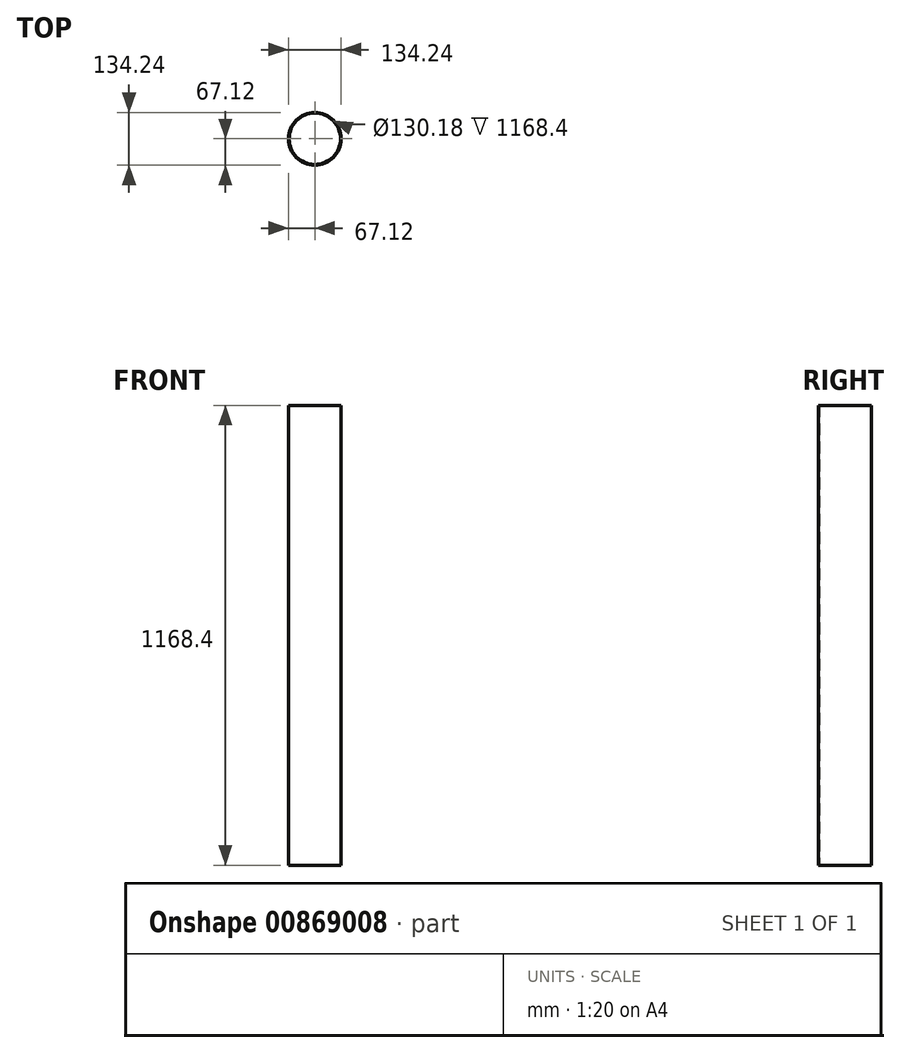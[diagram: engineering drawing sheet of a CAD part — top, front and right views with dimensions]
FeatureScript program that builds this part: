
annotation { "Feature Type Name" : "Feature", "Feature Type Description" : "" }
export const myFeature = defineFeature(function(context is Context, id is Id, definition is map)
    precondition{}
    {
        {
            var Q0;
            Q0=qCreatedBy(makeId("Top.planeOp"),FACE);
            var sketch = newSketch(context, id + "F0", { "sketchPlane" : qUnion([Q0]), "disableImprinting" : false});
            skCircle(sketch, "E0", {"center": v(0, 0) * mm, "radius": 65.09 * mm});
            skCircle(sketch, "E1.0", {"center": v(0, 0) * mm, "radius": 67.12 * mm});
            skSolve(sketch);
        }
        {
            var Q0;
            Q0 = qSketchRegion(id + "F0", true);
            extrude(context, id + "F1", {"entities" : qUnion([Q0]), "flatOperationType" : FlatOperationType.REMOVE, "depth" : 1168.4 * mm, "offsetDistance" : 25.4 * mm, "domain" : OperationDomain.MODEL});
        }
    });
